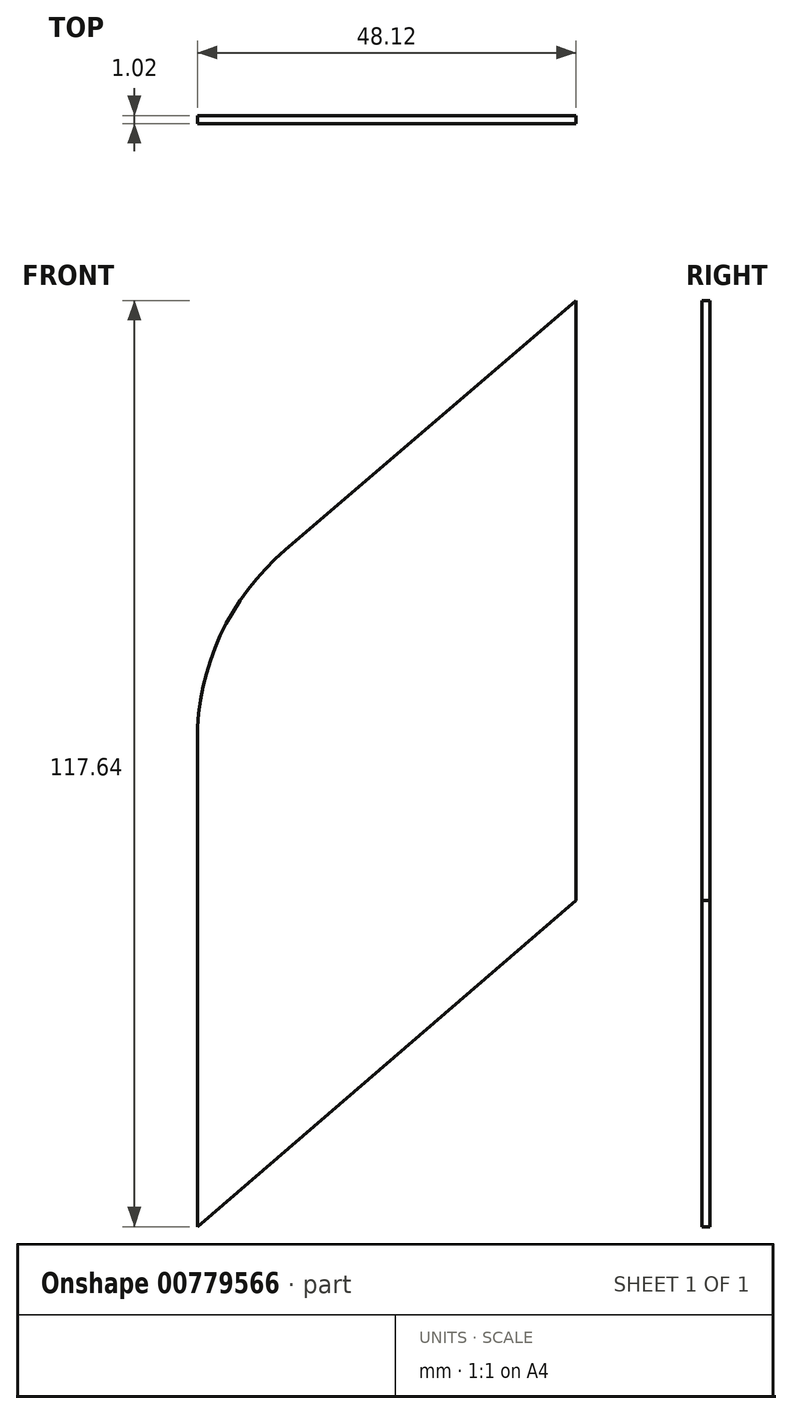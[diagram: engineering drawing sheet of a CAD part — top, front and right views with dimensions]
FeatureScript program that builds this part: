
annotation { "Feature Type Name" : "Feature", "Feature Type Description" : "" }
export const myFeature = defineFeature(function(context is Context, id is Id, definition is map)
    precondition{}
    {
        {
            var Q0;
            Q0=qCreatedBy(makeId("Front.planeOp"),FACE);
            var sketch = newSketch(context, id + "F0", { "sketchPlane" : qUnion([Q0])});
            skLineSegment(sketch, "E0", {"start": v(0, 0) * mm, "end": v(-48.12, -41.44) * mm});
            skLineSegment(sketch, "E1", {"start": v(-48.12, -41.44) * mm, "end": v(-48.12, 20.29) * mm});
            skLineSegment(sketch, "E2", {"start": v(-36.97, 44.52) * mm, "end": v(0, 76.2) * mm});
            skLineSegment(sketch, "E3", {"start": v(0, 76.2) * mm, "end": v(0, 0) * mm});
            skPoint(sketch, "E4.visualSharp", {"position": v(-48.12, 34.97) * mm});
            skArc(sketch, "E4.filletArc", {"start": v(-36.97, 44.52) * mm, "mid": v(-45.2, 33.63) * mm, "end": v(-48.12, 20.29) * mm});
            skSolve(sketch);
        }
        {
            var Q0;
            Q0 = qSketchRegion(id + "F0", true);
            extrude(context, id + "F1", {"entities" : qUnion([Q0]), "depth" : 1.02 * mm, "offsetDistance" : 25.4 * mm});
        }
    });
